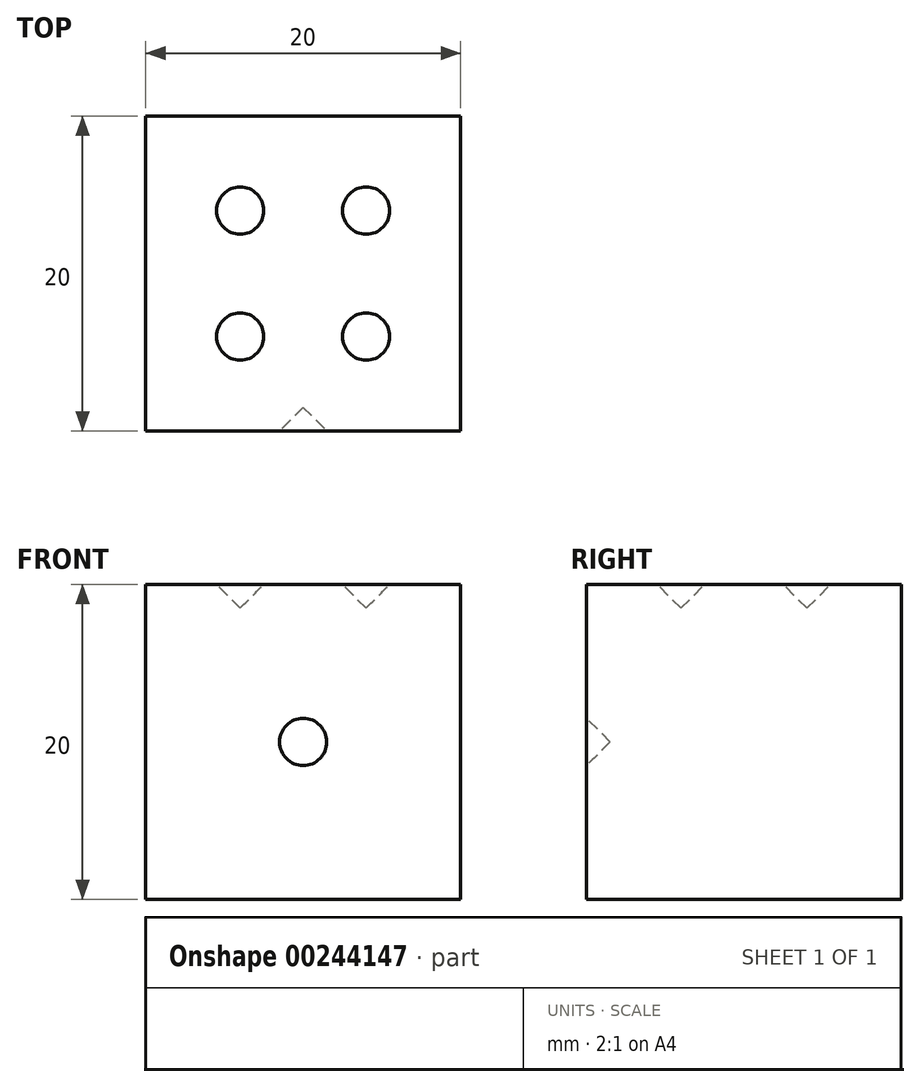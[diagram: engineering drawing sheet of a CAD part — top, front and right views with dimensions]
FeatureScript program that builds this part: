
annotation { "Feature Type Name" : "Feature", "Feature Type Description" : "" }
export const myFeature = defineFeature(function(context is Context, id is Id, definition is map)
    precondition{}
    {
        {
            var Q0;
            Q0=qCreatedBy(makeId("Top.planeOp"),FACE);
            var sketch = newSketch(context, id + "F0", { "sketchPlane" : qUnion([Q0])});
            skLineSegment(sketch, "E0.bottom", {"start": v(0, 0) * mm, "end": v(20, 0) * mm});
            skLineSegment(sketch, "E0.left", {"start": v(0, 0) * mm, "end": v(0, 20) * mm});
            skLineSegment(sketch, "E0.right", {"start": v(20, 0) * mm, "end": v(20, 20) * mm});
            skLineSegment(sketch, "E1", {"start": v(0, 20) * mm, "end": v(20, 20) * mm});
            skSolve(sketch);
        }
        {
            var Q0;
            Q0 = qSketchRegion(id + "F0", true);
            extrude(context, id + "F1", {"entities" : qUnion([Q0]), "depth" : 20 * mm});
        }
        {
            var Q0;
            Q0=makeQuery(id+"F1.opExtrude","SWEPT_FACE",FACE,{"disambiguationData":[OSD([sQuery(id+"F0.wireOp",EDGE,"E0.bottom")])]});
            var sketch = newSketch(context, id + "F2", { "sketchPlane" : qUnion([Q0])});
            skLineSegment(sketch, "E2.0", {"start": v(0, 0) * mm, "end": v(20, 0) * mm, "construction": true});
            skLineSegment(sketch, "E2.1", {"start": v(0, 20) * mm, "end": v(20, 20) * mm, "construction": true});
            skLineSegment(sketch, "E3", {"start": v(10, 20) * mm, "end": v(10, 0) * mm, "construction": true});
            skCircle(sketch, "E4", {"center": v(10, 10) * mm, "radius": 1.5 * mm});
            skSolve(sketch);
        }
        {
            var Q0;
            Q0=makeQuery(id+"F2.imprint","IMPRINT",FACE,{"disambiguationData":[TD([[makeQuery(id+"F2.imprint","IMPRINT",EDGE,{"derivedFrom":sQuery(id+"F2.wireOp",EDGE,"E4")}),1.0]])]});
            extrude(context, id + "F3", {"entities" : qUnion([Q0]), "operationType" : NewBodyOperationType.REMOVE, "oppositeDirection" : true, "depth" : 1.5 * mm});
        }
        {
            var Q0;
            Q0=makeQuery(id+"F1.opExtrude","CAP_FACE",FACE,{"disambiguationData":[OSD([sQuery(id+"F0.wireOp",EDGE,"E0.bottom"),sQuery(id+"F0.wireOp",EDGE,"E0.left"),sQuery(id+"F0.wireOp",EDGE,"E0.right"),sQuery(id+"F0.wireOp",EDGE,"E1")])],"isStart":false});
            var sketch = newSketch(context, id + "F4", { "sketchPlane" : qUnion([Q0])});
            skLineSegment(sketch, "E5.0", {"start": v(0, 20) * mm, "end": v(6, 20) * mm, "construction": true});
            skLineSegment(sketch, "E6", {"start": v(6, 20) * mm, "end": v(6, 14) * mm, "construction": true});
            skCircle(sketch, "E7", {"center": v(6, 6) * mm, "radius": 1.5 * mm});
            skCircle(sketch, "E8", {"center": v(6, 14) * mm, "radius": 1.5 * mm});
            skPoint(sketch, "E9.orphan", {"position": v(20, 20) * mm});
            skPoint(sketch, "E10.orphan", {"position": v(20, 0) * mm});
            skLineSegment(sketch, "E11", {"start": v(0, 0) * mm, "end": v(6, 0) * mm, "construction": true});
            skLineSegment(sketch, "E12", {"start": v(6, 0) * mm, "end": v(6, 6) * mm, "construction": true});
            skLineSegment(sketch, "E13.0", {"start": v(0, 20) * mm, "end": v(20, 20) * mm, "construction": true});
            skLineSegment(sketch, "E13.1", {"start": v(0, 0) * mm, "end": v(20, 0) * mm, "construction": true});
            skLineSegment(sketch, "E14", {"start": v(10, 20) * mm, "end": v(10, 0) * mm, "construction": true});
            skCircle(sketch, "E15.MirrorC", {"center": v(14, 6) * mm, "radius": 1.5 * mm});
            skCircle(sketch, "E16.MirrorC", {"center": v(14, 14) * mm, "radius": 1.5 * mm});
            skSolve(sketch);
        }
        {
            var Q0;
            Q0 = qSketchRegion(id + "F4", true);
            extrude(context, id + "F5", {"entities" : qUnion([Q0]), "operationType" : NewBodyOperationType.REMOVE, "oppositeDirection" : true, "depth" : 1.5 * mm});
        }
        {
            var Q0;
            Q0=makeQuery(id+"F3.boolean.opBoolean","COPY",EDGE,{"derivedFrom":makeQuery(id+"F3.opExtrude","CAP_EDGE",EDGE,{"disambiguationData":[OSD([sQuery(id+"F2.wireOp",EDGE,"E4")])],"isStart":false})});
            var Q1;
            Q1=makeQuery(id+"F5.boolean.opBoolean","COPY",EDGE,{"derivedFrom":makeQuery(id+"F5.opExtrude","CAP_EDGE",EDGE,{"disambiguationData":[OSD([sQuery(id+"F4.wireOp",EDGE,"E7")])],"isStart":false})});
            var Q2;
            Q2=makeQuery(id+"F5.boolean.opBoolean","COPY",EDGE,{"derivedFrom":makeQuery(id+"F5.opExtrude","CAP_EDGE",EDGE,{"disambiguationData":[OSD([sQuery(id+"F4.wireOp",EDGE,"E8")])],"isStart":false})});
            var Q3;
            Q3=makeQuery(id+"F5.boolean.opBoolean","COPY",EDGE,{"derivedFrom":makeQuery(id+"F5.opExtrude","CAP_EDGE",EDGE,{"disambiguationData":[OSD([sQuery(id+"F4.wireOp",EDGE,"E16.MirrorC")])],"isStart":false})});
            var Q4;
            Q4=makeQuery(id+"F5.boolean.opBoolean","COPY",EDGE,{"derivedFrom":makeQuery(id+"F5.opExtrude","CAP_EDGE",EDGE,{"disambiguationData":[OSD([sQuery(id+"F4.wireOp",EDGE,"E15.MirrorC")])],"isStart":false})});
            chamfer(context, id + "F6", {"entities" : qUnion([Q0, Q1, Q2, Q3, Q4]), "width" : 1.5 * mm, "tangentPropagation" : true});
        }
    });
